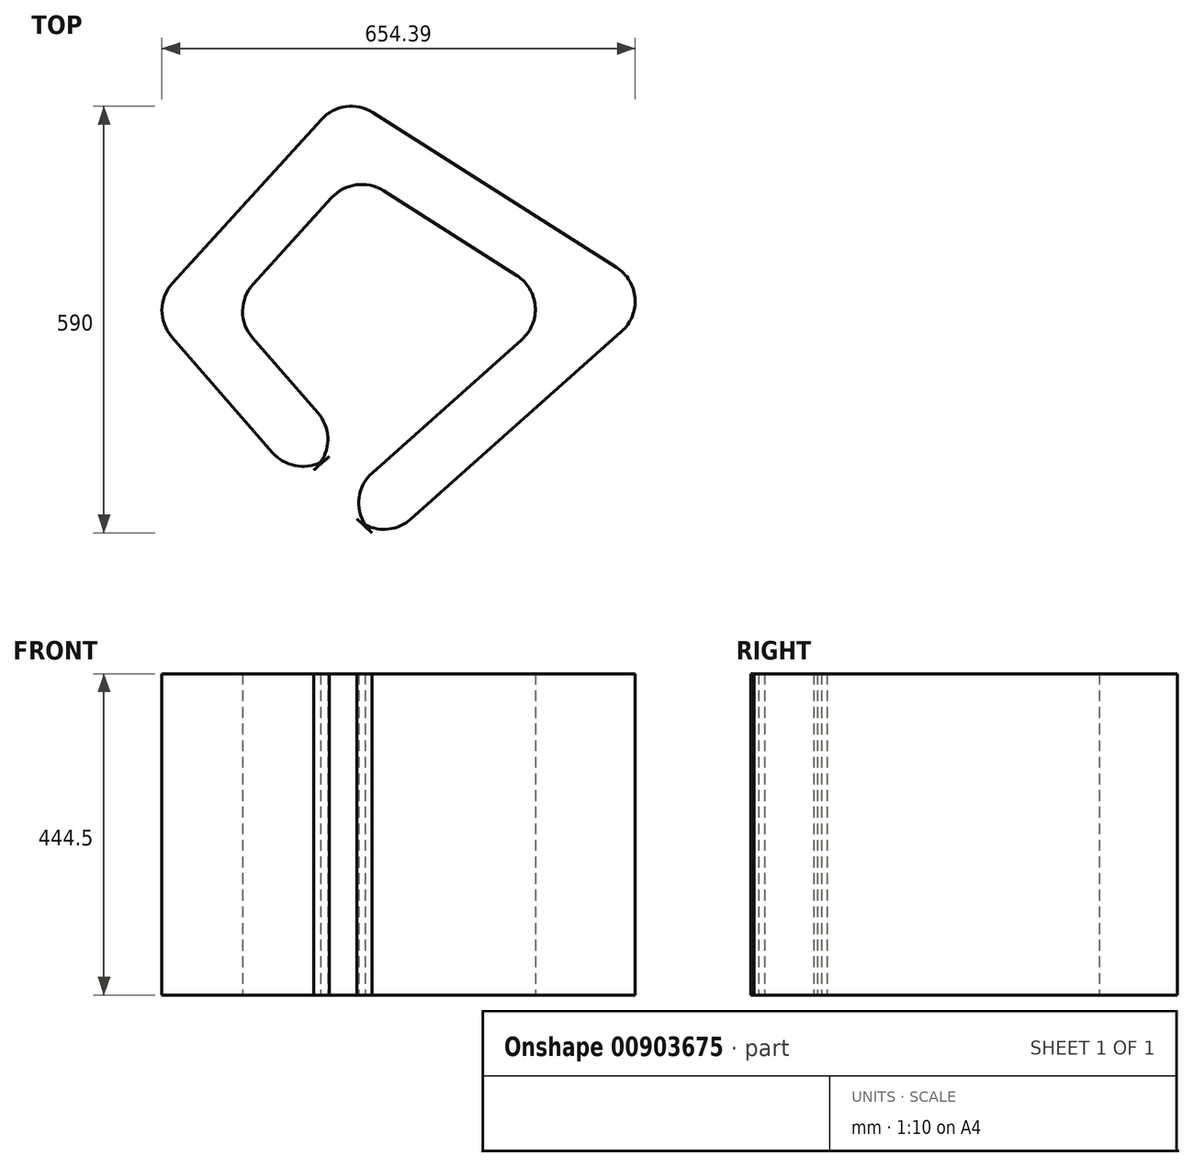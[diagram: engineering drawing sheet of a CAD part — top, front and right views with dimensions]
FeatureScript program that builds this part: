
annotation { "Feature Type Name" : "Feature", "Feature Type Description" : "" }
export const myFeature = defineFeature(function(context is Context, id is Id, definition is map)
    precondition{}
    {
        {
            var Q0;
            Q0=qCreatedBy(makeId("Top.planeOp"),FACE);
            var sketch = newSketch(context, id + "F0", { "sketchPlane" : qUnion([Q0])});
            skLineSegment(sketch, "E0", {"start": v(-109.95, -150.92) * mm, "end": v(-249, 9.04) * mm});
            skLineSegment(sketch, "E1", {"start": v(-248.16, 83.3) * mm, "end": v(-42.24, 309.72) * mm});
            skLineSegment(sketch, "E2", {"start": v(29.07, 319.29) * mm, "end": v(365.78, 105.35) * mm});
            skLineSegment(sketch, "E3", {"start": v(372.97, 16.46) * mm, "end": v(81.43, -243.17) * mm});
            skLineSegment(sketch, "E4.0", {"start": v(235, 5.29) * mm, "end": v(28.25, -178.82) * mm});
            skLineSegment(sketch, "E4.1", {"start": v(43.57, 211.24) * mm, "end": v(227.8, 94.18) * mm});
            skLineSegment(sketch, "E4.2", {"start": v(-136.54, 82.04) * mm, "end": v(-27.74, 201.67) * mm});
            skLineSegment(sketch, "E4.3", {"start": v(-47, -96.2) * mm, "end": v(-137.37, 7.78) * mm});
            skLineSegment(sketch, "E5", {"start": v(-52.5, -175.03) * mm, "end": v(-31.12, -156.44) * mm});
            skLineSegment(sketch, "E6", {"start": v(27.93, -262) * mm, "end": v(6.79, -242.88) * mm});
            skPoint(sketch, "E7.visualSharp", {"position": v(-10.33, -138.37) * mm});
            skArc(sketch, "E7.filletArc", {"start": v(-52.5, -175.03) * mm, "mid": v(-33.42, -136.75) * mm, "end": v(-47, -96.2) * mm});
            skPoint(sketch, "E8.visualSharp", {"position": v(-73.3, -193.1) * mm});
            skArc(sketch, "E8.filletArc", {"start": v(-109.95, -150.92) * mm, "mid": v(-71.68, -170) * mm, "end": v(-31.12, -156.44) * mm});
            skPoint(sketch, "E9.visualSharp", {"position": v(-18.25, -220.23) * mm});
            skArc(sketch, "E9.filletArc", {"start": v(28.25, -178.82) * mm, "mid": v(9.53, -220.34) * mm, "end": v(27.93, -262) * mm});
            skPoint(sketch, "E10.visualSharp", {"position": v(43.98, -276.52) * mm});
            skArc(sketch, "E10.filletArc", {"start": v(6.79, -242.88) * mm, "mid": v(44.05, -257.31) * mm, "end": v(81.43, -243.17) * mm});
            skPoint(sketch, "E11.visualSharp", {"position": v(428.23, 65.67) * mm});
            skArc(sketch, "E11.filletArc", {"start": v(372.97, 16.46) * mm, "mid": v(391.5, 62.7) * mm, "end": v(365.78, 105.35) * mm});
            skPoint(sketch, "E12.visualSharp", {"position": v(290.25, 54.5) * mm});
            skArc(sketch, "E12.filletArc", {"start": v(235, 5.29) * mm, "mid": v(253.53, 51.53) * mm, "end": v(227.8, 94.18) * mm});
            skPoint(sketch, "E13.visualSharp", {"position": v(-10.61, 344.5) * mm});
            skArc(sketch, "E13.filletArc", {"start": v(29.07, 319.29) * mm, "mid": v(-8.33, 327.5) * mm, "end": v(-42.24, 309.72) * mm});
            skPoint(sketch, "E14.visualSharp", {"position": v(3.89, 236.45) * mm});
            skArc(sketch, "E14.filletArc", {"start": v(43.57, 211.24) * mm, "mid": v(6.17, 219.46) * mm, "end": v(-27.74, 201.67) * mm});
            skPoint(sketch, "E15.visualSharp", {"position": v(-169.96, 45.28) * mm});
            skArc(sketch, "E15.filletArc", {"start": v(-136.54, 82.04) * mm, "mid": v(-151.07, 45.07) * mm, "end": v(-137.37, 7.78) * mm});
            skPoint(sketch, "E16.visualSharp", {"position": v(-281.58, 46.53) * mm});
            skArc(sketch, "E16.filletArc", {"start": v(-248.16, 83.3) * mm, "mid": v(-262.7, 46.32) * mm, "end": v(-249, 9.04) * mm});
            skSolve(sketch);
        }
        {
            var Q0;
            Q0 = qSketchRegion(id + "F0", true);
            var Q1;
            Q1=sQuery(id+"F0.wireOp",EDGE,"E0");
            var Q2;
            Q2=sQuery(id+"F0.wireOp",EDGE,"E1");
            var Q3;
            Q3=sQuery(id+"F0.wireOp",EDGE,"E2");
            var Q4;
            Q4=sQuery(id+"F0.wireOp",EDGE,"E3");
            extrude(context, id + "F1", {"entities" : qUnion([Q0]), "bodyType" : ToolBodyType.SURFACE, "surfaceEntities" : qUnion([Q1, Q2, Q3, Q4]), "depth" : 444.5 * mm, "offsetDistance" : 25.4 * mm});
        }
        {
            var Q0;
            Q0 = qSketchRegion(id + "F0", true);
            extrude(context, id + "F2", {"entities" : qUnion([Q0]), "depth" : 444.5 * mm, "offsetDistance" : 25.4 * mm});
        }
    });
